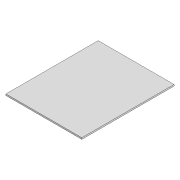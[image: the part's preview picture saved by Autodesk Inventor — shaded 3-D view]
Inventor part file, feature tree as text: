
AUTODESK INVENTOR PART (.ipt)
format: ipt  version: 2020 (Build 240168000, 168)  size: 74,240 bytes
history: native  units: in
note: dims shown in document units (in); Inventor stores cm internally (conversion verified against a paired STEP export)
features: extrude x1, sketch x1
ambient origin geometry x8: Origin, YZ Plane, XZ Plane, XY Plane, X Axis, Y Axis, Z Axis, Center Point
bodies: Solid1 (feature_tree)
feature tree (2):
  extrude  "Extrusion1"  Depth=12.2047in
  sketch  "Sketch1"  dims[d0=10.0394in d1=12.2047in d2=0.1969in d3=0.0in]
